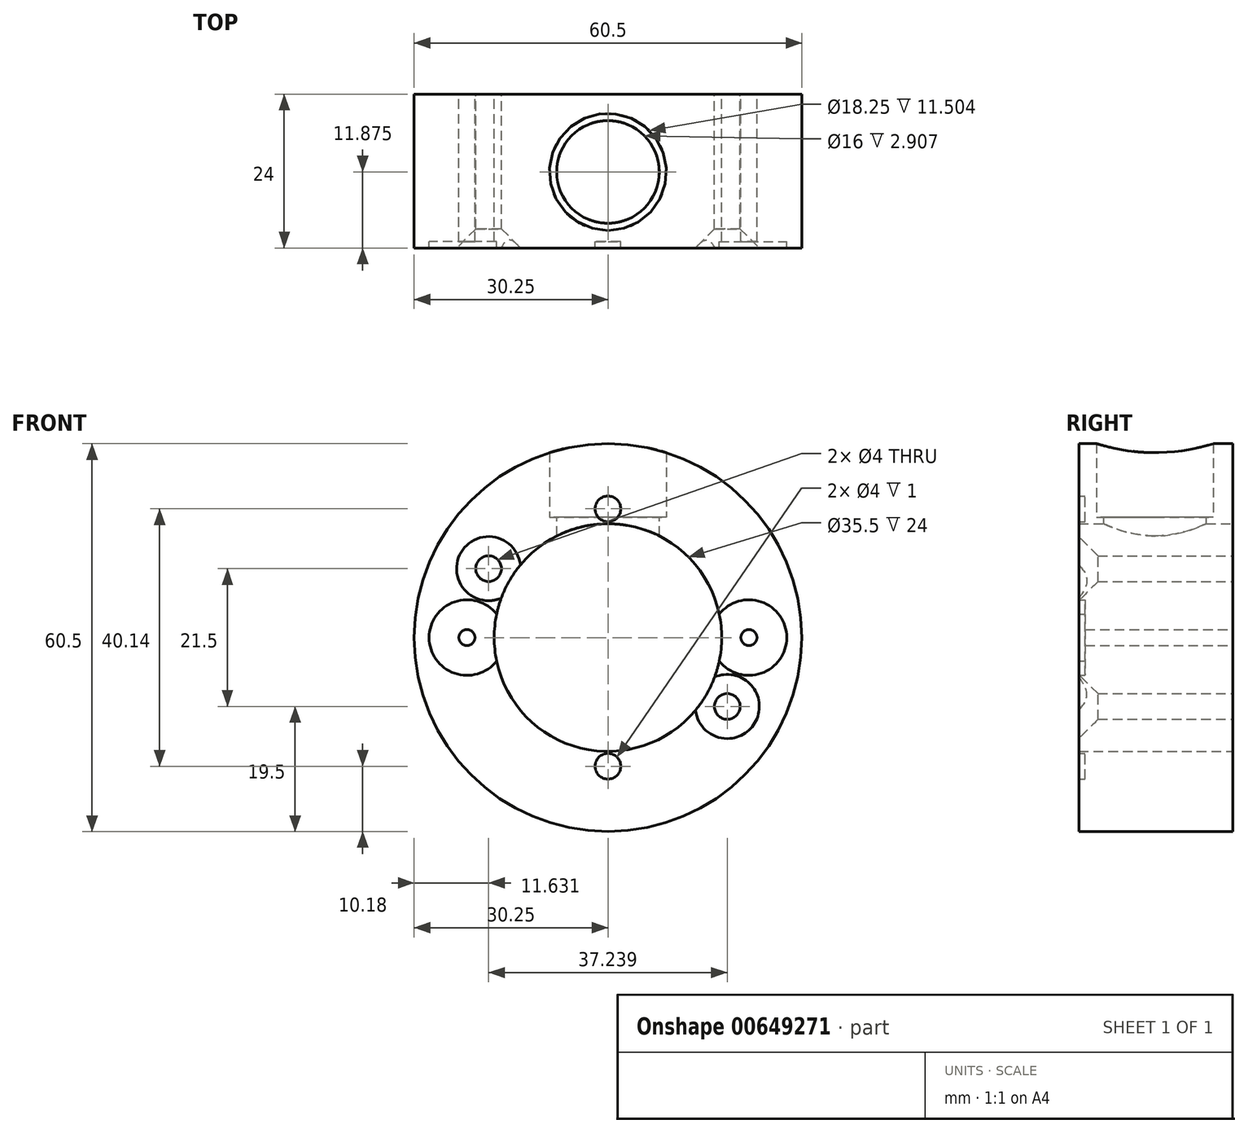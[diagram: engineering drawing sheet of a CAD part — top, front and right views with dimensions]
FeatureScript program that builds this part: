
annotation { "Feature Type Name" : "Feature", "Feature Type Description" : "" }
export const myFeature = defineFeature(function(context is Context, id is Id, definition is map)
    precondition{}
    {
        {
            var Q0;
            Q0=qCreatedBy(makeId("Front.planeOp"),FACE);
            var sketch = newSketch(context, id + "F0", { "sketchPlane" : qUnion([Q0])});
            skCircle(sketch, "E0", {"center": v(0, 0) * mm, "radius": 30.25 * mm});
            skCircle(sketch, "E1.0", {"center": v(0, 0) * mm, "radius": 17.75 * mm});
            skCircle(sketch, "E2", {"center": v(-22, 0) * mm, "radius": 1.25 * mm});
            skCircle(sketch, "E3", {"center": v(22, 0) * mm, "radius": 1.25 * mm});
            skCircle(sketch, "E4", {"center": v(-22, 0) * mm, "radius": 5.9 * mm});
            skCircle(sketch, "E5", {"center": v(22, 0) * mm, "radius": 5.9 * mm});
            skCircle(sketch, "E6", {"center": v(-18.62, 10.75) * mm, "radius": 2 * mm});
            skCircle(sketch, "E7", {"center": v(18.62, -10.75) * mm, "radius": 2 * mm});
            skLineSegment(sketch, "E8", {"start": v(0, 0) * mm, "end": v(-18.62, 10.75) * mm});
            skLineSegment(sketch, "E9", {"start": v(0, 0) * mm, "end": v(8.87, 15.37) * mm});
            skCircle(sketch, "E10", {"center": v(0, -20.07) * mm, "radius": 2 * mm});
            skCircle(sketch, "E11", {"center": v(0, 20.07) * mm, "radius": 2 * mm});
            skSolve(sketch);
        }
        {
            var Q0;
            Q0=qSketchRegion(id+"F0",true);
            extrude(context, id + "F1", {"entities" : qUnion([Q0]), "depth" : 24 * mm, "offsetDistance" : 25 * mm});
        }
        {
            var Q0;
            Q0=makeQuery(id+"F0.imprint","IMPRINT",FACE,{"disambiguationData":[TD([[makeQuery(id+"F0.imprint","IMPRINT",EDGE,{"derivedFrom":sQuery(id+"F0.wireOp",EDGE,"E2")}),-1.0]])]});
            var Q1;
            Q1=makeQuery(id+"F0.imprint","IMPRINT",FACE,{"disambiguationData":[TD([[makeQuery(id+"F0.imprint","IMPRINT",EDGE,{"derivedFrom":sQuery(id+"F0.wireOp",EDGE,"E11")}),1.0]])]});
            var Q2;
            Q2=makeQuery(id+"F0.imprint","IMPRINT",FACE,{"disambiguationData":[TD([[makeQuery(id+"F0.imprint","IMPRINT",EDGE,{"derivedFrom":sQuery(id+"F0.wireOp",EDGE,"E3")}),-1.0]])]});
            var Q3;
            Q3=makeQuery(id+"F0.imprint","IMPRINT",FACE,{"disambiguationData":[TD([[makeQuery(id+"F0.imprint","IMPRINT",EDGE,{"derivedFrom":sQuery(id+"F0.wireOp",EDGE,"E10")}),1.0]])]});
            extrude(context, id + "F2", {"entities" : qUnion([Q0, Q1, Q2, Q3]), "operationType" : NewBodyOperationType.ADD, "depth" : 23 * mm, "offsetDistance" : 25 * mm});
        }
        {
            var Q0;
            Q0=makeQuery(id+"F1.opExtrude","CAP_EDGE",EDGE,{"disambiguationData":[OSD([sQuery(id+"F0.wireOp",EDGE,"E6")])],"isStart":false});
            var Q1;
            Q1=makeQuery(id+"F1.opExtrude","CAP_EDGE",EDGE,{"disambiguationData":[OSD([sQuery(id+"F0.wireOp",EDGE,"E7")])],"isStart":false});
            chamfer(context, id + "F3", {"entities" : qUnion([Q0, Q1]), "width" : 3 * mm, "tangentPropagation" : true});
        }
        {
            var Q0;
            Q0=qCreatedBy(makeId("Top.planeOp"),FACE);
            cPlane(context, id + "F4", {"entities" : qUnion([Q0]), "cplaneType" : CPlaneType.OFFSET, "offset" : 18.75 * mm, "width" : 150 * mm, "height" : 150 * mm});
        }
        {
            var Q0;
            Q0=qCreatedBy(id+"F4.planeOp",FACE);
            var sketch = newSketch(context, id + "F5", { "sketchPlane" : qUnion([Q0])});
            skCircle(sketch, "E12", {"center": v(0, -12.12) * mm, "radius": 9.12 * mm});
            skCircle(sketch, "E13", {"center": v(0, -12.12) * mm, "radius": 8 * mm});
            skSolve(sketch);
        }
        {
            var Q0;
            Q0=qSketchRegion(id+"F5",true);
            extrude(context, id + "F6", {"entities" : qUnion([Q0]), "operationType" : NewBodyOperationType.REMOVE, "oppositeDirection" : true, "depth" : -25 * mm, "offsetDistance" : 25 * mm});
        }
        {
            var Q0;
            Q0=makeQuery(id+"F5.imprint","IMPRINT",FACE,{"disambiguationData":[TD([[makeQuery(id+"F5.imprint","IMPRINT",EDGE,{"derivedFrom":sQuery(id+"F5.wireOp",EDGE,"E13")}),1.0]])]});
            extrude(context, id + "F7", {"entities" : qUnion([Q0]), "operationType" : NewBodyOperationType.REMOVE, "endBound" : BoundingType.SYMMETRIC, "oppositeDirection" : true, "depth" : 30 * mm, "offsetDistance" : 25 * mm});
        }
    });
